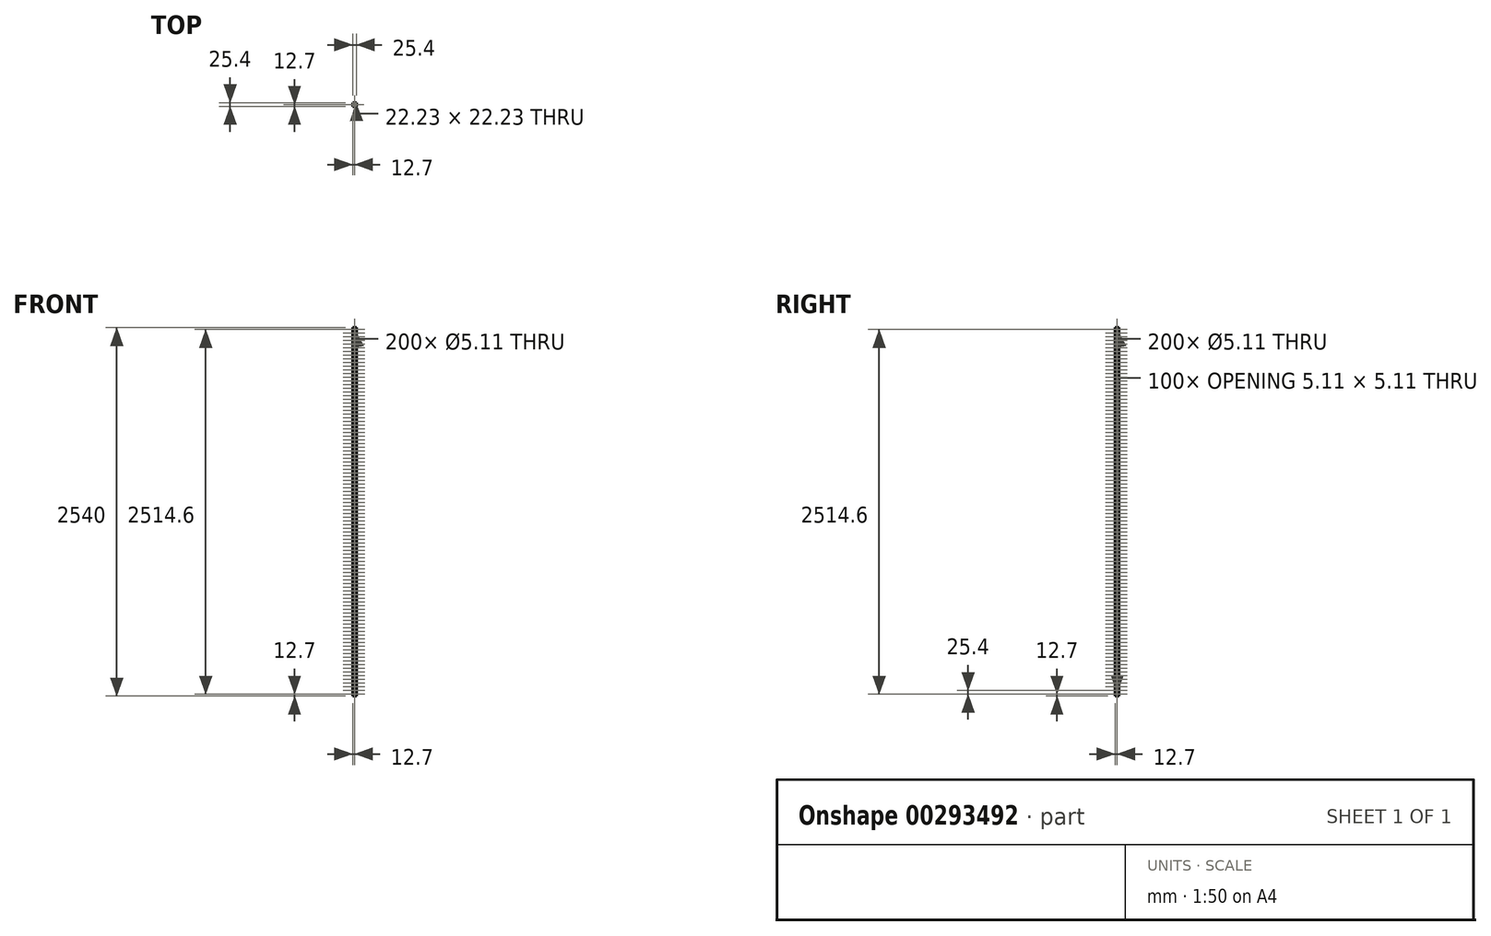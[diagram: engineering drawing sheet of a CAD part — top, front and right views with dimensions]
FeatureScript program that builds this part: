
annotation { "Feature Type Name" : "Feature", "Feature Type Description" : "" }
export const myFeature = defineFeature(function(context is Context, id is Id, definition is map)
    precondition{}
    {
        {
            var Q0;
            Q0=qCreatedBy(makeId("Top.planeOp"),FACE);
            var sketch = newSketch(context, id + "F0", { "sketchPlane" : qUnion([Q0])});
            skLineSegment(sketch, "E0.bottom", {"start": v(12.7, -12.7) * mm, "end": v(-12.7, -12.7) * mm});
            skLineSegment(sketch, "E0.top", {"start": v(12.7, 12.7) * mm, "end": v(-12.7, 12.7) * mm});
            skLineSegment(sketch, "E0.left", {"start": v(12.7, -12.7) * mm, "end": v(12.7, 12.7) * mm});
            skLineSegment(sketch, "E0.right", {"start": v(-12.7, -12.7) * mm, "end": v(-12.7, 12.7) * mm});
            skPoint(sketch, "E0.middle", {"position": v(0, 0) * mm});
            skSolve(sketch);
        }
        {
            var Q0;
            Q0=makeQuery(id+"F0.imprint","IMPRINT",FACE,{"disambiguationData":[TD([[makeQuery(id+"F0.imprint","IMPRINT",EDGE,{"derivedFrom":sQuery(id+"F0.wireOp",EDGE,"E0.bottom")}),-1.0]])]});
            extrude(context, id + "F1", {"entities" : qUnion([Q0]), "depth" : 2540 * mm});
        }
        {
            var Q0;
            Q0=makeQuery(id+"F1.opExtrude","SWEPT_FACE",FACE,{"disambiguationData":[OSD([sQuery(id+"F0.wireOp",EDGE,"E0.top")])]});
            var sketch = newSketch(context, id + "F2", { "sketchPlane" : qUnion([Q0])});
            skCircle(sketch, "E1", {"center": v(0, 2527.3) * mm, "radius": 2.55 * mm});
            skCircle(sketch, "E2.1.0.0", {"center": v(0, 2501.9) * mm, "radius": 2.55 * mm});
            skCircle(sketch, "E2.2.0.0", {"center": v(0, 2476.5) * mm, "radius": 2.55 * mm});
            skCircle(sketch, "E2.3.0.0", {"center": v(0, 2451.1) * mm, "radius": 2.55 * mm});
            skCircle(sketch, "E2.4.0.0", {"center": v(0, 2425.7) * mm, "radius": 2.55 * mm});
            skCircle(sketch, "E2.5.0.0", {"center": v(0, 2400.3) * mm, "radius": 2.55 * mm});
            skCircle(sketch, "E2.6.0.0", {"center": v(0, 2374.9) * mm, "radius": 2.55 * mm});
            skCircle(sketch, "E2.7.0.0", {"center": v(0, 2349.5) * mm, "radius": 2.55 * mm});
            skCircle(sketch, "E2.8.0.0", {"center": v(0, 2324.1) * mm, "radius": 2.55 * mm});
            skCircle(sketch, "E2.9.0.0", {"center": v(0, 2298.7) * mm, "radius": 2.55 * mm});
            skCircle(sketch, "E2.10.0.0", {"center": v(0, 2273.3) * mm, "radius": 2.55 * mm});
            skCircle(sketch, "E2.11.0.0", {"center": v(0, 2247.9) * mm, "radius": 2.55 * mm});
            skCircle(sketch, "E2.12.0.0", {"center": v(0, 2222.5) * mm, "radius": 2.55 * mm});
            skCircle(sketch, "E2.13.0.0", {"center": v(0, 2197.1) * mm, "radius": 2.55 * mm});
            skCircle(sketch, "E2.14.0.0", {"center": v(0, 2171.7) * mm, "radius": 2.55 * mm});
            skCircle(sketch, "E2.15.0.0", {"center": v(0, 2146.3) * mm, "radius": 2.55 * mm});
            skCircle(sketch, "E2.16.0.0", {"center": v(0, 2120.9) * mm, "radius": 2.55 * mm});
            skCircle(sketch, "E2.17.0.0", {"center": v(0, 2095.5) * mm, "radius": 2.55 * mm});
            skCircle(sketch, "E2.18.0.0", {"center": v(0, 2070.1) * mm, "radius": 2.55 * mm});
            skCircle(sketch, "E2.19.0.0", {"center": v(0, 2044.7) * mm, "radius": 2.55 * mm});
            skCircle(sketch, "E2.20.0.0", {"center": v(0, 2019.3) * mm, "radius": 2.55 * mm});
            skCircle(sketch, "E2.21.0.0", {"center": v(0, 1993.9) * mm, "radius": 2.55 * mm});
            skCircle(sketch, "E2.22.0.0", {"center": v(0, 1968.5) * mm, "radius": 2.55 * mm});
            skCircle(sketch, "E2.23.0.0", {"center": v(0, 1943.1) * mm, "radius": 2.55 * mm});
            skCircle(sketch, "E2.24.0.0", {"center": v(0, 1917.7) * mm, "radius": 2.55 * mm});
            skCircle(sketch, "E2.25.0.0", {"center": v(0, 1892.3) * mm, "radius": 2.55 * mm});
            skCircle(sketch, "E2.26.0.0", {"center": v(0, 1866.9) * mm, "radius": 2.55 * mm});
            skCircle(sketch, "E2.27.0.0", {"center": v(0, 1841.5) * mm, "radius": 2.55 * mm});
            skCircle(sketch, "E2.28.0.0", {"center": v(0, 1816.1) * mm, "radius": 2.55 * mm});
            skCircle(sketch, "E2.29.0.0", {"center": v(0, 1790.7) * mm, "radius": 2.55 * mm});
            skCircle(sketch, "E2.30.0.0", {"center": v(0, 1765.3) * mm, "radius": 2.55 * mm});
            skCircle(sketch, "E2.31.0.0", {"center": v(0, 1739.9) * mm, "radius": 2.55 * mm});
            skCircle(sketch, "E2.32.0.0", {"center": v(0, 1714.5) * mm, "radius": 2.55 * mm});
            skCircle(sketch, "E2.33.0.0", {"center": v(0, 1689.1) * mm, "radius": 2.55 * mm});
            skCircle(sketch, "E2.34.0.0", {"center": v(0, 1663.7) * mm, "radius": 2.55 * mm});
            skCircle(sketch, "E2.35.0.0", {"center": v(0, 1638.3) * mm, "radius": 2.55 * mm});
            skCircle(sketch, "E2.36.0.0", {"center": v(0, 1612.9) * mm, "radius": 2.55 * mm});
            skCircle(sketch, "E2.37.0.0", {"center": v(0, 1587.5) * mm, "radius": 2.55 * mm});
            skCircle(sketch, "E2.38.0.0", {"center": v(0, 1562.1) * mm, "radius": 2.55 * mm});
            skCircle(sketch, "E2.39.0.0", {"center": v(0, 1536.7) * mm, "radius": 2.55 * mm});
            skCircle(sketch, "E2.40.0.0", {"center": v(0, 1511.3) * mm, "radius": 2.55 * mm});
            skCircle(sketch, "E2.41.0.0", {"center": v(0, 1485.9) * mm, "radius": 2.55 * mm});
            skCircle(sketch, "E2.42.0.0", {"center": v(0, 1460.5) * mm, "radius": 2.55 * mm});
            skCircle(sketch, "E2.43.0.0", {"center": v(0, 1435.1) * mm, "radius": 2.55 * mm});
            skCircle(sketch, "E2.44.0.0", {"center": v(0, 1409.7) * mm, "radius": 2.55 * mm});
            skCircle(sketch, "E2.45.0.0", {"center": v(0, 1384.3) * mm, "radius": 2.55 * mm});
            skCircle(sketch, "E2.46.0.0", {"center": v(0, 1358.9) * mm, "radius": 2.55 * mm});
            skCircle(sketch, "E2.47.0.0", {"center": v(0, 1333.5) * mm, "radius": 2.55 * mm});
            skCircle(sketch, "E2.48.0.0", {"center": v(0, 1308.1) * mm, "radius": 2.55 * mm});
            skCircle(sketch, "E2.49.0.0", {"center": v(0, 1282.7) * mm, "radius": 2.55 * mm});
            skCircle(sketch, "E2.50.0.0", {"center": v(0, 1257.3) * mm, "radius": 2.55 * mm});
            skCircle(sketch, "E2.51.0.0", {"center": v(0, 1231.9) * mm, "radius": 2.55 * mm});
            skCircle(sketch, "E2.52.0.0", {"center": v(0, 1206.5) * mm, "radius": 2.55 * mm});
            skCircle(sketch, "E2.53.0.0", {"center": v(0, 1181.1) * mm, "radius": 2.55 * mm});
            skCircle(sketch, "E2.54.0.0", {"center": v(0, 1155.7) * mm, "radius": 2.55 * mm});
            skCircle(sketch, "E2.55.0.0", {"center": v(0, 1130.3) * mm, "radius": 2.55 * mm});
            skCircle(sketch, "E2.56.0.0", {"center": v(0, 1104.9) * mm, "radius": 2.55 * mm});
            skCircle(sketch, "E2.57.0.0", {"center": v(0, 1079.5) * mm, "radius": 2.55 * mm});
            skCircle(sketch, "E2.58.0.0", {"center": v(0, 1054.1) * mm, "radius": 2.55 * mm});
            skCircle(sketch, "E2.59.0.0", {"center": v(0, 1028.7) * mm, "radius": 2.55 * mm});
            skCircle(sketch, "E2.60.0.0", {"center": v(0, 1003.3) * mm, "radius": 2.55 * mm});
            skCircle(sketch, "E2.61.0.0", {"center": v(0, 977.9) * mm, "radius": 2.55 * mm});
            skCircle(sketch, "E2.62.0.0", {"center": v(0, 952.5) * mm, "radius": 2.55 * mm});
            skCircle(sketch, "E2.63.0.0", {"center": v(0, 927.1) * mm, "radius": 2.55 * mm});
            skCircle(sketch, "E2.64.0.0", {"center": v(0, 901.7) * mm, "radius": 2.55 * mm});
            skCircle(sketch, "E2.65.0.0", {"center": v(0, 876.3) * mm, "radius": 2.55 * mm});
            skCircle(sketch, "E2.66.0.0", {"center": v(0, 850.9) * mm, "radius": 2.55 * mm});
            skCircle(sketch, "E2.67.0.0", {"center": v(0, 825.5) * mm, "radius": 2.55 * mm});
            skCircle(sketch, "E2.68.0.0", {"center": v(0, 800.1) * mm, "radius": 2.55 * mm});
            skCircle(sketch, "E2.69.0.0", {"center": v(0, 774.7) * mm, "radius": 2.55 * mm});
            skCircle(sketch, "E2.70.0.0", {"center": v(0, 749.3) * mm, "radius": 2.55 * mm});
            skCircle(sketch, "E2.71.0.0", {"center": v(0, 723.9) * mm, "radius": 2.55 * mm});
            skCircle(sketch, "E2.72.0.0", {"center": v(0, 698.5) * mm, "radius": 2.55 * mm});
            skCircle(sketch, "E2.73.0.0", {"center": v(0, 673.1) * mm, "radius": 2.55 * mm});
            skCircle(sketch, "E2.74.0.0", {"center": v(0, 647.7) * mm, "radius": 2.55 * mm});
            skCircle(sketch, "E2.75.0.0", {"center": v(0, 622.3) * mm, "radius": 2.55 * mm});
            skCircle(sketch, "E2.76.0.0", {"center": v(0, 596.9) * mm, "radius": 2.55 * mm});
            skCircle(sketch, "E2.77.0.0", {"center": v(0, 571.5) * mm, "radius": 2.55 * mm});
            skCircle(sketch, "E2.78.0.0", {"center": v(0, 546.1) * mm, "radius": 2.55 * mm});
            skCircle(sketch, "E2.79.0.0", {"center": v(0, 520.7) * mm, "radius": 2.55 * mm});
            skCircle(sketch, "E2.80.0.0", {"center": v(0, 495.3) * mm, "radius": 2.55 * mm});
            skCircle(sketch, "E2.81.0.0", {"center": v(0, 469.9) * mm, "radius": 2.55 * mm});
            skCircle(sketch, "E2.82.0.0", {"center": v(0, 444.5) * mm, "radius": 2.55 * mm});
            skCircle(sketch, "E2.83.0.0", {"center": v(0, 419.1) * mm, "radius": 2.55 * mm});
            skCircle(sketch, "E2.84.0.0", {"center": v(0, 393.7) * mm, "radius": 2.55 * mm});
            skCircle(sketch, "E2.85.0.0", {"center": v(0, 368.3) * mm, "radius": 2.55 * mm});
            skCircle(sketch, "E2.86.0.0", {"center": v(0, 342.9) * mm, "radius": 2.55 * mm});
            skCircle(sketch, "E2.87.0.0", {"center": v(0, 317.5) * mm, "radius": 2.55 * mm});
            skCircle(sketch, "E2.88.0.0", {"center": v(0, 292.1) * mm, "radius": 2.55 * mm});
            skCircle(sketch, "E2.89.0.0", {"center": v(0, 266.7) * mm, "radius": 2.55 * mm});
            skCircle(sketch, "E2.90.0.0", {"center": v(0, 241.3) * mm, "radius": 2.55 * mm});
            skCircle(sketch, "E2.91.0.0", {"center": v(0, 215.9) * mm, "radius": 2.55 * mm});
            skCircle(sketch, "E2.92.0.0", {"center": v(0, 190.5) * mm, "radius": 2.55 * mm});
            skCircle(sketch, "E2.93.0.0", {"center": v(0, 165.1) * mm, "radius": 2.55 * mm});
            skCircle(sketch, "E2.94.0.0", {"center": v(0, 139.7) * mm, "radius": 2.55 * mm});
            skCircle(sketch, "E2.95.0.0", {"center": v(0, 114.3) * mm, "radius": 2.55 * mm});
            skCircle(sketch, "E2.96.0.0", {"center": v(0, 88.9) * mm, "radius": 2.55 * mm});
            skCircle(sketch, "E2.97.0.0", {"center": v(0, 63.5) * mm, "radius": 2.55 * mm});
            skCircle(sketch, "E2.98.0.0", {"center": v(0, 38.1) * mm, "radius": 2.55 * mm});
            skCircle(sketch, "E2.99.0.0", {"center": v(0, 12.7) * mm, "radius": 2.55 * mm});
            skLineSegment(sketch, "E2.direction1", {"start": v(0, 2527.3) * mm, "end": v(0, 2501.9) * mm, "construction": true});
            skSolve(sketch);
        }
        {
            var Q0;
            Q0=makeQuery(id+"F1.opExtrude","SWEPT_FACE",FACE,{"disambiguationData":[OSD([sQuery(id+"F0.wireOp",EDGE,"E0.right")])]});
            var sketch = newSketch(context, id + "F3", { "sketchPlane" : qUnion([Q0])});
            skCircle(sketch, "E3", {"center": v(0, 2527.3) * mm, "radius": 2.55 * mm});
            skCircle(sketch, "E4.1.0.0", {"center": v(0, 2501.9) * mm, "radius": 2.55 * mm});
            skCircle(sketch, "E4.2.0.0", {"center": v(0, 2476.5) * mm, "radius": 2.55 * mm});
            skCircle(sketch, "E4.3.0.0", {"center": v(0, 2451.1) * mm, "radius": 2.55 * mm});
            skCircle(sketch, "E4.4.0.0", {"center": v(0, 2425.7) * mm, "radius": 2.55 * mm});
            skCircle(sketch, "E4.5.0.0", {"center": v(0, 2400.3) * mm, "radius": 2.55 * mm});
            skCircle(sketch, "E4.6.0.0", {"center": v(0, 2374.9) * mm, "radius": 2.55 * mm});
            skCircle(sketch, "E4.7.0.0", {"center": v(0, 2349.5) * mm, "radius": 2.55 * mm});
            skCircle(sketch, "E4.8.0.0", {"center": v(0, 2324.1) * mm, "radius": 2.55 * mm});
            skCircle(sketch, "E4.9.0.0", {"center": v(0, 2298.7) * mm, "radius": 2.55 * mm});
            skCircle(sketch, "E4.10.0.0", {"center": v(0, 2273.3) * mm, "radius": 2.55 * mm});
            skCircle(sketch, "E4.11.0.0", {"center": v(0, 2247.9) * mm, "radius": 2.55 * mm});
            skCircle(sketch, "E4.12.0.0", {"center": v(0, 2222.5) * mm, "radius": 2.55 * mm});
            skCircle(sketch, "E4.13.0.0", {"center": v(0, 2197.1) * mm, "radius": 2.55 * mm});
            skCircle(sketch, "E4.14.0.0", {"center": v(0, 2171.7) * mm, "radius": 2.55 * mm});
            skCircle(sketch, "E4.15.0.0", {"center": v(0, 2146.3) * mm, "radius": 2.55 * mm});
            skCircle(sketch, "E4.16.0.0", {"center": v(0, 2120.9) * mm, "radius": 2.55 * mm});
            skCircle(sketch, "E4.17.0.0", {"center": v(0, 2095.5) * mm, "radius": 2.55 * mm});
            skCircle(sketch, "E4.18.0.0", {"center": v(0, 2070.1) * mm, "radius": 2.55 * mm});
            skCircle(sketch, "E4.19.0.0", {"center": v(0, 2044.7) * mm, "radius": 2.55 * mm});
            skCircle(sketch, "E4.20.0.0", {"center": v(0, 2019.3) * mm, "radius": 2.55 * mm});
            skCircle(sketch, "E4.21.0.0", {"center": v(0, 1993.9) * mm, "radius": 2.55 * mm});
            skCircle(sketch, "E4.22.0.0", {"center": v(0, 1968.5) * mm, "radius": 2.55 * mm});
            skCircle(sketch, "E4.23.0.0", {"center": v(0, 1943.1) * mm, "radius": 2.55 * mm});
            skCircle(sketch, "E4.24.0.0", {"center": v(0, 1917.7) * mm, "radius": 2.55 * mm});
            skCircle(sketch, "E4.25.0.0", {"center": v(0, 1892.3) * mm, "radius": 2.55 * mm});
            skCircle(sketch, "E4.26.0.0", {"center": v(0, 1866.9) * mm, "radius": 2.55 * mm});
            skCircle(sketch, "E4.27.0.0", {"center": v(0, 1841.5) * mm, "radius": 2.55 * mm});
            skCircle(sketch, "E4.28.0.0", {"center": v(0, 1816.1) * mm, "radius": 2.55 * mm});
            skCircle(sketch, "E4.29.0.0", {"center": v(0, 1790.7) * mm, "radius": 2.55 * mm});
            skCircle(sketch, "E4.30.0.0", {"center": v(0, 1765.3) * mm, "radius": 2.55 * mm});
            skCircle(sketch, "E4.31.0.0", {"center": v(0, 1739.9) * mm, "radius": 2.55 * mm});
            skCircle(sketch, "E4.32.0.0", {"center": v(0, 1714.5) * mm, "radius": 2.55 * mm});
            skCircle(sketch, "E4.33.0.0", {"center": v(0, 1689.1) * mm, "radius": 2.55 * mm});
            skCircle(sketch, "E4.34.0.0", {"center": v(0, 1663.7) * mm, "radius": 2.55 * mm});
            skCircle(sketch, "E4.35.0.0", {"center": v(0, 1638.3) * mm, "radius": 2.55 * mm});
            skCircle(sketch, "E4.36.0.0", {"center": v(0, 1612.9) * mm, "radius": 2.55 * mm});
            skCircle(sketch, "E4.37.0.0", {"center": v(0, 1587.5) * mm, "radius": 2.55 * mm});
            skCircle(sketch, "E4.38.0.0", {"center": v(0, 1562.1) * mm, "radius": 2.55 * mm});
            skCircle(sketch, "E4.39.0.0", {"center": v(0, 1536.7) * mm, "radius": 2.55 * mm});
            skCircle(sketch, "E4.40.0.0", {"center": v(0, 1511.3) * mm, "radius": 2.55 * mm});
            skCircle(sketch, "E4.41.0.0", {"center": v(0, 1485.9) * mm, "radius": 2.55 * mm});
            skCircle(sketch, "E4.42.0.0", {"center": v(0, 1460.5) * mm, "radius": 2.55 * mm});
            skCircle(sketch, "E4.43.0.0", {"center": v(0, 1435.1) * mm, "radius": 2.55 * mm});
            skCircle(sketch, "E4.44.0.0", {"center": v(0, 1409.7) * mm, "radius": 2.55 * mm});
            skCircle(sketch, "E4.45.0.0", {"center": v(0, 1384.3) * mm, "radius": 2.55 * mm});
            skCircle(sketch, "E4.46.0.0", {"center": v(0, 1358.9) * mm, "radius": 2.55 * mm});
            skCircle(sketch, "E4.47.0.0", {"center": v(0, 1333.5) * mm, "radius": 2.55 * mm});
            skCircle(sketch, "E4.48.0.0", {"center": v(0, 1308.1) * mm, "radius": 2.55 * mm});
            skCircle(sketch, "E4.49.0.0", {"center": v(0, 1282.7) * mm, "radius": 2.55 * mm});
            skCircle(sketch, "E4.50.0.0", {"center": v(0, 1257.3) * mm, "radius": 2.55 * mm});
            skCircle(sketch, "E4.51.0.0", {"center": v(0, 1231.9) * mm, "radius": 2.55 * mm});
            skCircle(sketch, "E4.52.0.0", {"center": v(0, 1206.5) * mm, "radius": 2.55 * mm});
            skCircle(sketch, "E4.53.0.0", {"center": v(0, 1181.1) * mm, "radius": 2.55 * mm});
            skCircle(sketch, "E4.54.0.0", {"center": v(0, 1155.7) * mm, "radius": 2.55 * mm});
            skCircle(sketch, "E4.55.0.0", {"center": v(0, 1130.3) * mm, "radius": 2.55 * mm});
            skCircle(sketch, "E4.56.0.0", {"center": v(0, 1104.9) * mm, "radius": 2.55 * mm});
            skCircle(sketch, "E4.57.0.0", {"center": v(0, 1079.5) * mm, "radius": 2.55 * mm});
            skCircle(sketch, "E4.58.0.0", {"center": v(0, 1054.1) * mm, "radius": 2.55 * mm});
            skCircle(sketch, "E4.59.0.0", {"center": v(0, 1028.7) * mm, "radius": 2.55 * mm});
            skCircle(sketch, "E4.60.0.0", {"center": v(0, 1003.3) * mm, "radius": 2.55 * mm});
            skCircle(sketch, "E4.61.0.0", {"center": v(0, 977.9) * mm, "radius": 2.55 * mm});
            skCircle(sketch, "E4.62.0.0", {"center": v(0, 952.5) * mm, "radius": 2.55 * mm});
            skCircle(sketch, "E4.63.0.0", {"center": v(0, 927.1) * mm, "radius": 2.55 * mm});
            skCircle(sketch, "E4.64.0.0", {"center": v(0, 901.7) * mm, "radius": 2.55 * mm});
            skCircle(sketch, "E4.65.0.0", {"center": v(0, 876.3) * mm, "radius": 2.55 * mm});
            skCircle(sketch, "E4.66.0.0", {"center": v(0, 850.9) * mm, "radius": 2.55 * mm});
            skCircle(sketch, "E4.67.0.0", {"center": v(0, 825.5) * mm, "radius": 2.55 * mm});
            skCircle(sketch, "E4.68.0.0", {"center": v(0, 800.1) * mm, "radius": 2.55 * mm});
            skCircle(sketch, "E4.69.0.0", {"center": v(0, 774.7) * mm, "radius": 2.55 * mm});
            skCircle(sketch, "E4.70.0.0", {"center": v(0, 749.3) * mm, "radius": 2.55 * mm});
            skCircle(sketch, "E4.71.0.0", {"center": v(0, 723.9) * mm, "radius": 2.55 * mm});
            skCircle(sketch, "E4.72.0.0", {"center": v(0, 698.5) * mm, "radius": 2.55 * mm});
            skCircle(sketch, "E4.73.0.0", {"center": v(0, 673.1) * mm, "radius": 2.55 * mm});
            skCircle(sketch, "E4.74.0.0", {"center": v(0, 647.7) * mm, "radius": 2.55 * mm});
            skCircle(sketch, "E4.75.0.0", {"center": v(0, 622.3) * mm, "radius": 2.55 * mm});
            skCircle(sketch, "E4.76.0.0", {"center": v(0, 596.9) * mm, "radius": 2.55 * mm});
            skCircle(sketch, "E4.77.0.0", {"center": v(0, 571.5) * mm, "radius": 2.55 * mm});
            skCircle(sketch, "E4.78.0.0", {"center": v(0, 546.1) * mm, "radius": 2.55 * mm});
            skCircle(sketch, "E4.79.0.0", {"center": v(0, 520.7) * mm, "radius": 2.55 * mm});
            skCircle(sketch, "E4.80.0.0", {"center": v(0, 495.3) * mm, "radius": 2.55 * mm});
            skCircle(sketch, "E4.81.0.0", {"center": v(0, 469.9) * mm, "radius": 2.55 * mm});
            skCircle(sketch, "E4.82.0.0", {"center": v(0, 444.5) * mm, "radius": 2.55 * mm});
            skCircle(sketch, "E4.83.0.0", {"center": v(0, 419.1) * mm, "radius": 2.55 * mm});
            skCircle(sketch, "E4.84.0.0", {"center": v(0, 393.7) * mm, "radius": 2.55 * mm});
            skCircle(sketch, "E4.85.0.0", {"center": v(0, 368.3) * mm, "radius": 2.55 * mm});
            skCircle(sketch, "E4.86.0.0", {"center": v(0, 342.9) * mm, "radius": 2.55 * mm});
            skCircle(sketch, "E4.87.0.0", {"center": v(0, 317.5) * mm, "radius": 2.55 * mm});
            skCircle(sketch, "E4.88.0.0", {"center": v(0, 292.1) * mm, "radius": 2.55 * mm});
            skCircle(sketch, "E4.89.0.0", {"center": v(0, 266.7) * mm, "radius": 2.55 * mm});
            skCircle(sketch, "E4.90.0.0", {"center": v(0, 241.3) * mm, "radius": 2.55 * mm});
            skCircle(sketch, "E4.91.0.0", {"center": v(0, 215.9) * mm, "radius": 2.55 * mm});
            skCircle(sketch, "E4.92.0.0", {"center": v(0, 190.5) * mm, "radius": 2.55 * mm});
            skCircle(sketch, "E4.93.0.0", {"center": v(0, 165.1) * mm, "radius": 2.55 * mm});
            skCircle(sketch, "E4.94.0.0", {"center": v(0, 139.7) * mm, "radius": 2.55 * mm});
            skCircle(sketch, "E4.95.0.0", {"center": v(0, 114.3) * mm, "radius": 2.55 * mm});
            skCircle(sketch, "E4.96.0.0", {"center": v(0, 88.9) * mm, "radius": 2.55 * mm});
            skCircle(sketch, "E4.97.0.0", {"center": v(0, 63.5) * mm, "radius": 2.55 * mm});
            skCircle(sketch, "E4.98.0.0", {"center": v(0, 38.1) * mm, "radius": 2.55 * mm});
            skCircle(sketch, "E4.99.0.0", {"center": v(0, 12.7) * mm, "radius": 2.55 * mm});
            skLineSegment(sketch, "E4.direction1", {"start": v(0, 2527.3) * mm, "end": v(0, 2501.9) * mm, "construction": true});
            skSolve(sketch);
        }
        {
            var Q0;
            Q0=makeQuery(id+"F1.opExtrude","CAP_FACE",FACE,{"disambiguationData":[OSD([sQuery(id+"F0.wireOp",EDGE,"E0.bottom"),sQuery(id+"F0.wireOp",EDGE,"E0.top"),sQuery(id+"F0.wireOp",EDGE,"E0.left"),sQuery(id+"F0.wireOp",EDGE,"E0.right")])],"isStart":false});
            var sketch = newSketch(context, id + "F4", { "sketchPlane" : qUnion([Q0])});
            skLineSegment(sketch, "E5.bottom", {"start": v(11.11, -11.11) * mm, "end": v(-11.11, -11.11) * mm});
            skLineSegment(sketch, "E5.top", {"start": v(11.11, 11.11) * mm, "end": v(-11.11, 11.11) * mm});
            skLineSegment(sketch, "E5.left", {"start": v(11.11, -11.11) * mm, "end": v(11.11, 11.11) * mm});
            skLineSegment(sketch, "E5.right", {"start": v(-11.11, -11.11) * mm, "end": v(-11.11, 11.11) * mm});
            skPoint(sketch, "E5.middle", {"position": v(0, 0) * mm});
            skSolve(sketch);
        }
        {
            var Q0;
            Q0=makeQuery(id+"F4.imprint","IMPRINT",FACE,{"disambiguationData":[TD([[makeQuery(id+"F4.imprint","IMPRINT",EDGE,{"derivedFrom":sQuery(id+"F4.wireOp",EDGE,"E5.bottom")}),-1.0]])]});
            extrude(context, id + "F5", {"entities" : qUnion([Q0]), "operationType" : NewBodyOperationType.REMOVE, "oppositeDirection" : true, "depth" : 2540 * mm});
        }
        {
            var Q0;
            Q0=sQuery(id+"F2.wireOp",VERTEX,"E2.99.0.0.center");
            var Q1;
            Q1=sQuery(id+"F2.wireOp",VERTEX,"E2.79.0.0.center");
            var Q2;
            Q2=sQuery(id+"F2.wireOp",VERTEX,"E2.63.0.0.center");
            var Q3;
            Q3=sQuery(id+"F2.wireOp",VERTEX,"E2.47.0.0.center");
            var Q4;
            Q4=sQuery(id+"F2.wireOp",VERTEX,"E2.31.0.0.center");
            var Q5;
            Q5=sQuery(id+"F2.wireOp",VERTEX,"E2.95.0.0.center");
            var Q6;
            Q6=sQuery(id+"F2.wireOp",VERTEX,"E2.54.0.0.center");
            var Q7;
            Q7=sQuery(id+"F2.wireOp",VERTEX,"E2.38.0.0.center");
            var Q8;
            Q8=sQuery(id+"F2.wireOp",VERTEX,"E2.22.0.0.center");
            var Q9;
            Q9=sQuery(id+"F2.wireOp",VERTEX,"E2.86.0.0.center");
            var Q10;
            Q10=sQuery(id+"F2.wireOp",VERTEX,"E2.70.0.0.center");
            var Q11;
            Q11=sQuery(id+"F2.wireOp",VERTEX,"E2.80.0.0.center");
            var Q12;
            Q12=sQuery(id+"F2.wireOp",VERTEX,"E2.13.0.0.center");
            var Q13;
            Q13=sQuery(id+"F2.wireOp",VERTEX,"E2.64.0.0.center");
            var Q14;
            Q14=sQuery(id+"F2.wireOp",VERTEX,"E2.96.0.0.center");
            var Q15;
            Q15=sQuery(id+"F2.wireOp",VERTEX,"E1.center");
            var Q16;
            Q16=sQuery(id+"F2.wireOp",VERTEX,"E2.1.0.0.center");
            var Q17;
            Q17=sQuery(id+"F2.wireOp",VERTEX,"E2.2.0.0.center");
            var Q18;
            Q18=sQuery(id+"F2.wireOp",VERTEX,"E2.3.0.0.center");
            var Q19;
            Q19=sQuery(id+"F2.wireOp",VERTEX,"E2.4.0.0.center");
            var Q20;
            Q20=sQuery(id+"F2.wireOp",VERTEX,"E2.5.0.0.center");
            var Q21;
            Q21=sQuery(id+"F2.wireOp",VERTEX,"E2.6.0.0.center");
            var Q22;
            Q22=sQuery(id+"F2.wireOp",VERTEX,"E2.8.0.0.center");
            var Q23;
            Q23=sQuery(id+"F2.wireOp",VERTEX,"E2.9.0.0.center");
            var Q24;
            Q24=sQuery(id+"F2.wireOp",VERTEX,"E2.10.0.0.center");
            var Q25;
            Q25=sQuery(id+"F2.wireOp",VERTEX,"E2.55.0.0.center");
            var Q26;
            Q26=sQuery(id+"F2.wireOp",VERTEX,"E2.39.0.0.center");
            var Q27;
            Q27=sQuery(id+"F2.wireOp",VERTEX,"E2.87.0.0.center");
            var Q28;
            Q28=sQuery(id+"F2.wireOp",VERTEX,"E2.71.0.0.center");
            var Q29;
            Q29=sQuery(id+"F2.wireOp",VERTEX,"E2.17.0.0.center");
            var Q30;
            Q30=sQuery(id+"F2.wireOp",VERTEX,"E2.49.0.0.center");
            var Q31;
            Q31=sQuery(id+"F2.wireOp",VERTEX,"E2.33.0.0.center");
            var Q32;
            Q32=sQuery(id+"F2.wireOp",VERTEX,"E2.56.0.0.center");
            var Q33;
            Q33=sQuery(id+"F2.wireOp",VERTEX,"E2.40.0.0.center");
            var Q34;
            Q34=sQuery(id+"F2.wireOp",VERTEX,"E2.24.0.0.center");
            var Q35;
            Q35=sQuery(id+"F2.wireOp",VERTEX,"E2.88.0.0.center");
            var Q36;
            Q36=sQuery(id+"F2.wireOp",VERTEX,"E2.72.0.0.center");
            var Q37;
            Q37=sQuery(id+"F2.wireOp",VERTEX,"E2.18.0.0.center");
            var Q38;
            Q38=sQuery(id+"F2.wireOp",VERTEX,"E2.82.0.0.center");
            var Q39;
            Q39=sQuery(id+"F2.wireOp",VERTEX,"E2.75.0.0.center");
            var Q40;
            Q40=sQuery(id+"F2.wireOp",VERTEX,"E2.66.0.0.center");
            var Q41;
            Q41=sQuery(id+"F2.wireOp",VERTEX,"E2.59.0.0.center");
            var Q42;
            Q42=sQuery(id+"F2.wireOp",VERTEX,"E2.50.0.0.center");
            var Q43;
            Q43=sQuery(id+"F2.wireOp",VERTEX,"E2.43.0.0.center");
            var Q44;
            Q44=sQuery(id+"F2.wireOp",VERTEX,"E2.34.0.0.center");
            var Q45;
            Q45=sQuery(id+"F2.wireOp",VERTEX,"E2.27.0.0.center");
            var Q46;
            Q46=sQuery(id+"F2.wireOp",VERTEX,"E2.98.0.0.center");
            var Q47;
            Q47=sQuery(id+"F2.wireOp",VERTEX,"E2.91.0.0.center");
            var Q48;
            Q48=sQuery(id+"F2.wireOp",VERTEX,"E2.58.0.0.center");
            var Q49;
            Q49=sQuery(id+"F2.wireOp",VERTEX,"E2.42.0.0.center");
            var Q50;
            Q50=sQuery(id+"F2.wireOp",VERTEX,"E2.26.0.0.center");
            var Q51;
            Q51=sQuery(id+"F2.wireOp",VERTEX,"E2.90.0.0.center");
            var Q52;
            Q52=sQuery(id+"F2.wireOp",VERTEX,"E2.74.0.0.center");
            var Q53;
            Q53=sQuery(id+"F2.wireOp",VERTEX,"E2.20.0.0.center");
            var Q54;
            Q54=sQuery(id+"F2.wireOp",VERTEX,"E2.77.0.0.center");
            var Q55;
            Q55=sQuery(id+"F2.wireOp",VERTEX,"E2.61.0.0.center");
            var Q56;
            Q56=sQuery(id+"F2.wireOp",VERTEX,"E2.45.0.0.center");
            var Q57;
            Q57=sQuery(id+"F2.wireOp",VERTEX,"E2.29.0.0.center");
            var Q58;
            Q58=sQuery(id+"F2.wireOp",VERTEX,"E2.93.0.0.center");
            var Q59;
            Q59=sQuery(id+"F2.wireOp",VERTEX,"E2.85.0.0.center");
            var Q60;
            Q60=sQuery(id+"F2.wireOp",VERTEX,"E2.69.0.0.center");
            var Q61;
            Q61=sQuery(id+"F2.wireOp",VERTEX,"E2.78.0.0.center");
            var Q62;
            Q62=sQuery(id+"F2.wireOp",VERTEX,"E2.62.0.0.center");
            var Q63;
            Q63=sQuery(id+"F2.wireOp",VERTEX,"E2.46.0.0.center");
            var Q64;
            Q64=sQuery(id+"F2.wireOp",VERTEX,"E2.30.0.0.center");
            var Q65;
            Q65=sQuery(id+"F2.wireOp",VERTEX,"E2.94.0.0.center");
            var Q66;
            Q66=sQuery(id+"F2.wireOp",VERTEX,"E2.53.0.0.center");
            var Q67;
            Q67=sQuery(id+"F2.wireOp",VERTEX,"E2.37.0.0.center");
            var Q68;
            Q68=sQuery(id+"F2.wireOp",VERTEX,"E2.21.0.0.center");
            var Q69;
            Q69=sQuery(id+"F2.wireOp",VERTEX,"E2.16.0.0.center");
            var Q70;
            Q70=sQuery(id+"F2.wireOp",VERTEX,"E2.12.0.0.center");
            var Q71;
            Q71=sQuery(id+"F2.wireOp",VERTEX,"E2.48.0.0.center");
            var Q72;
            Q72=sQuery(id+"F2.wireOp",VERTEX,"E2.32.0.0.center");
            var Q73;
            Q73=sQuery(id+"F2.wireOp",VERTEX,"E2.7.0.0.center");
            var Q74;
            Q74=sQuery(id+"F2.wireOp",VERTEX,"E2.23.0.0.center");
            var Q75;
            Q75=sQuery(id+"F2.wireOp",VERTEX,"E2.81.0.0.center");
            var Q76;
            Q76=sQuery(id+"F2.wireOp",VERTEX,"E2.65.0.0.center");
            var Q77;
            Q77=sQuery(id+"F2.wireOp",VERTEX,"E2.97.0.0.center");
            var Q78;
            Q78=sQuery(id+"F2.wireOp",VERTEX,"E2.57.0.0.center");
            var Q79;
            Q79=sQuery(id+"F2.wireOp",VERTEX,"E2.41.0.0.center");
            var Q80;
            Q80=sQuery(id+"F2.wireOp",VERTEX,"E2.25.0.0.center");
            var Q81;
            Q81=sQuery(id+"F2.wireOp",VERTEX,"E2.89.0.0.center");
            var Q82;
            Q82=sQuery(id+"F2.wireOp",VERTEX,"E2.73.0.0.center");
            var Q83;
            Q83=sQuery(id+"F2.wireOp",VERTEX,"E2.19.0.0.center");
            var Q84;
            Q84=sQuery(id+"F2.wireOp",VERTEX,"E2.76.0.0.center");
            var Q85;
            Q85=sQuery(id+"F2.wireOp",VERTEX,"E2.83.0.0.center");
            var Q86;
            Q86=sQuery(id+"F2.wireOp",VERTEX,"E2.60.0.0.center");
            var Q87;
            Q87=sQuery(id+"F2.wireOp",VERTEX,"E2.67.0.0.center");
            var Q88;
            Q88=sQuery(id+"F2.wireOp",VERTEX,"E2.44.0.0.center");
            var Q89;
            Q89=sQuery(id+"F2.wireOp",VERTEX,"E2.51.0.0.center");
            var Q90;
            Q90=sQuery(id+"F2.wireOp",VERTEX,"E2.28.0.0.center");
            var Q91;
            Q91=sQuery(id+"F2.wireOp",VERTEX,"E2.35.0.0.center");
            var Q92;
            Q92=sQuery(id+"F2.wireOp",VERTEX,"E2.92.0.0.center");
            var Q93;
            Q93=sQuery(id+"F2.wireOp",VERTEX,"E2.84.0.0.center");
            var Q94;
            Q94=sQuery(id+"F2.wireOp",VERTEX,"E2.68.0.0.center");
            var Q95;
            Q95=sQuery(id+"F2.wireOp",VERTEX,"E2.52.0.0.center");
            var Q96;
            Q96=sQuery(id+"F2.wireOp",VERTEX,"E2.36.0.0.center");
            var Q97;
            Q97=sQuery(id+"F2.wireOp",VERTEX,"E2.15.0.0.center");
            var Q98;
            Q98=sQuery(id+"F2.wireOp",VERTEX,"E2.11.0.0.center");
            var Q99;
            Q99=sQuery(id+"F2.wireOp",VERTEX,"E2.14.0.0.center");
            var Q100;
            Q100=makeQuery(id+"F1.opExtrude","SWEPT_BODY",BODY,{"disambiguationData":[OSD([sQuery(id+"F0.wireOp",EDGE,"E0.bottom"),sQuery(id+"F0.wireOp",EDGE,"E0.top"),sQuery(id+"F0.wireOp",EDGE,"E0.left"),sQuery(id+"F0.wireOp",EDGE,"E0.right")])]});
            hole(context, id + "F6", {"style" : HoleStyle.SIMPLE, "endStyle" : HoleEndStyle.THROUGH, "holeDiameter" : 5.1 * mm, "tappedDepth" : 12.7 * mm, "tapClearance" : 3, "locations" : qUnion([Q0, Q1, Q2, Q3, Q4, Q5, Q6, Q7, Q8, Q9, Q10, Q11, Q12, Q13, Q14, Q15, Q16, Q17, Q18, Q19, Q20, Q21, Q22, Q23, Q24, Q25, Q26, Q27, Q28, Q29, Q30, Q31, Q32, Q33, Q34, Q35, Q36, Q37, Q38, Q39, Q40, Q41, Q42, Q43, Q44, Q45, Q46, Q47, Q48, Q49, Q50, Q51, Q52, Q53, Q54, Q55, Q56, Q57, Q58, Q59, Q60, Q61, Q62, Q63, Q64, Q65, Q66, Q67, Q68, Q69, Q70, Q71, Q72, Q73, Q74, Q75, Q76, Q77, Q78, Q79, Q80, Q81, Q82, Q83, Q84, Q85, Q86, Q87, Q88, Q89, Q90, Q91, Q92, Q93, Q94, Q95, Q96, Q97, Q98, Q99]), "scope" : qUnion([Q100])});
        }
        {
            var Q0;
            Q0=sQuery(id+"F3.wireOp",VERTEX,"E4.48.0.0.center");
            var Q1;
            Q1=sQuery(id+"F3.wireOp",VERTEX,"E4.96.0.0.center");
            var Q2;
            Q2=sQuery(id+"F3.wireOp",VERTEX,"E4.55.0.0.center");
            var Q3;
            Q3=sQuery(id+"F3.wireOp",VERTEX,"E4.33.0.0.center");
            var Q4;
            Q4=sQuery(id+"F3.wireOp",VERTEX,"E4.97.0.0.center");
            var Q5;
            Q5=sQuery(id+"F3.wireOp",VERTEX,"E4.81.0.0.center");
            var Q6;
            Q6=sQuery(id+"F3.wireOp",VERTEX,"E4.65.0.0.center");
            var Q7;
            Q7=sQuery(id+"F3.wireOp",VERTEX,"E4.13.0.0.center");
            var Q8;
            Q8=sQuery(id+"F3.wireOp",VERTEX,"E3.center");
            var Q9;
            Q9=sQuery(id+"F3.wireOp",VERTEX,"E4.24.0.0.center");
            var Q10;
            Q10=sQuery(id+"F3.wireOp",VERTEX,"E4.2.0.0.center");
            var Q11;
            Q11=sQuery(id+"F3.wireOp",VERTEX,"E4.88.0.0.center");
            var Q12;
            Q12=sQuery(id+"F3.wireOp",VERTEX,"E4.3.0.0.center");
            var Q13;
            Q13=sQuery(id+"F3.wireOp",VERTEX,"E4.72.0.0.center");
            var Q14;
            Q14=sQuery(id+"F3.wireOp",VERTEX,"E4.40.0.0.center");
            var Q15;
            Q15=sQuery(id+"F3.wireOp",VERTEX,"E4.4.0.0.center");
            var Q16;
            Q16=sQuery(id+"F3.wireOp",VERTEX,"E4.5.0.0.center");
            var Q17;
            Q17=sQuery(id+"F3.wireOp",VERTEX,"E4.6.0.0.center");
            var Q18;
            Q18=sQuery(id+"F3.wireOp",VERTEX,"E4.7.0.0.center");
            var Q19;
            Q19=sQuery(id+"F3.wireOp",VERTEX,"E4.50.0.0.center");
            var Q20;
            Q20=sQuery(id+"F3.wireOp",VERTEX,"E4.34.0.0.center");
            var Q21;
            Q21=sQuery(id+"F3.wireOp",VERTEX,"E4.18.0.0.center");
            var Q22;
            Q22=sQuery(id+"F3.wireOp",VERTEX,"E4.9.0.0.center");
            var Q23;
            Q23=sQuery(id+"F3.wireOp",VERTEX,"E4.82.0.0.center");
            var Q24;
            Q24=sQuery(id+"F3.wireOp",VERTEX,"E4.66.0.0.center");
            var Q25;
            Q25=sQuery(id+"F3.wireOp",VERTEX,"E4.10.0.0.center");
            var Q26;
            Q26=sQuery(id+"F3.wireOp",VERTEX,"E4.25.0.0.center");
            var Q27;
            Q27=sQuery(id+"F3.wireOp",VERTEX,"E4.89.0.0.center");
            var Q28;
            Q28=sQuery(id+"F3.wireOp",VERTEX,"E4.73.0.0.center");
            var Q29;
            Q29=sQuery(id+"F3.wireOp",VERTEX,"E4.57.0.0.center");
            var Q30;
            Q30=sQuery(id+"F3.wireOp",VERTEX,"E4.41.0.0.center");
            var Q31;
            Q31=sQuery(id+"F3.wireOp",VERTEX,"E4.44.0.0.center");
            var Q32;
            Q32=sQuery(id+"F3.wireOp",VERTEX,"E4.51.0.0.center");
            var Q33;
            Q33=sQuery(id+"F3.wireOp",VERTEX,"E4.28.0.0.center");
            var Q34;
            Q34=sQuery(id+"F3.wireOp",VERTEX,"E4.35.0.0.center");
            var Q35;
            Q35=sQuery(id+"F3.wireOp",VERTEX,"E4.19.0.0.center");
            var Q36;
            Q36=sQuery(id+"F3.wireOp",VERTEX,"E4.92.0.0.center");
            var Q37;
            Q37=sQuery(id+"F3.wireOp",VERTEX,"E4.99.0.0.center");
            var Q38;
            Q38=sQuery(id+"F3.wireOp",VERTEX,"E4.76.0.0.center");
            var Q39;
            Q39=sQuery(id+"F3.wireOp",VERTEX,"E4.83.0.0.center");
            var Q40;
            Q40=sQuery(id+"F3.wireOp",VERTEX,"E4.60.0.0.center");
            var Q41;
            Q41=sQuery(id+"F3.wireOp",VERTEX,"E4.67.0.0.center");
            var Q42;
            Q42=sQuery(id+"F3.wireOp",VERTEX,"E4.68.0.0.center");
            var Q43;
            Q43=sQuery(id+"F3.wireOp",VERTEX,"E4.85.0.0.center");
            var Q44;
            Q44=sQuery(id+"F3.wireOp",VERTEX,"E4.69.0.0.center");
            var Q45;
            Q45=sQuery(id+"F3.wireOp",VERTEX,"E4.37.0.0.center");
            var Q46;
            Q46=sQuery(id+"F3.wireOp",VERTEX,"E4.21.0.0.center");
            var Q47;
            Q47=sQuery(id+"F3.wireOp",VERTEX,"E4.47.0.0.center");
            var Q48;
            Q48=sQuery(id+"F3.wireOp",VERTEX,"E4.95.0.0.center");
            var Q49;
            Q49=sQuery(id+"F3.wireOp",VERTEX,"E4.86.0.0.center");
            var Q50;
            Q50=sQuery(id+"F3.wireOp",VERTEX,"E4.54.0.0.center");
            var Q51;
            Q51=sQuery(id+"F3.wireOp",VERTEX,"E4.38.0.0.center");
            var Q52;
            Q52=sQuery(id+"F3.wireOp",VERTEX,"E4.32.0.0.center");
            var Q53;
            Q53=sQuery(id+"F3.wireOp",VERTEX,"E4.80.0.0.center");
            var Q54;
            Q54=sQuery(id+"F3.wireOp",VERTEX,"E4.64.0.0.center");
            var Q55;
            Q55=sQuery(id+"F3.wireOp",VERTEX,"E4.23.0.0.center");
            var Q56;
            Q56=sQuery(id+"F3.wireOp",VERTEX,"E4.87.0.0.center");
            var Q57;
            Q57=sQuery(id+"F3.wireOp",VERTEX,"E4.71.0.0.center");
            var Q58;
            Q58=sQuery(id+"F3.wireOp",VERTEX,"E4.39.0.0.center");
            var Q59;
            Q59=sQuery(id+"F3.wireOp",VERTEX,"E4.49.0.0.center");
            var Q60;
            Q60=sQuery(id+"F3.wireOp",VERTEX,"E4.17.0.0.center");
            var Q61;
            Q61=sQuery(id+"F3.wireOp",VERTEX,"E4.12.0.0.center");
            var Q62;
            Q62=sQuery(id+"F3.wireOp",VERTEX,"E4.1.0.0.center");
            var Q63;
            Q63=sQuery(id+"F3.wireOp",VERTEX,"E4.56.0.0.center");
            var Q64;
            Q64=sQuery(id+"F3.wireOp",VERTEX,"E4.8.0.0.center");
            var Q65;
            Q65=sQuery(id+"F3.wireOp",VERTEX,"E4.43.0.0.center");
            var Q66;
            Q66=sQuery(id+"F3.wireOp",VERTEX,"E4.27.0.0.center");
            var Q67;
            Q67=sQuery(id+"F3.wireOp",VERTEX,"E4.91.0.0.center");
            var Q68;
            Q68=sQuery(id+"F3.wireOp",VERTEX,"E4.98.0.0.center");
            var Q69;
            Q69=sQuery(id+"F3.wireOp",VERTEX,"E4.75.0.0.center");
            var Q70;
            Q70=sQuery(id+"F3.wireOp",VERTEX,"E4.59.0.0.center");
            var Q71;
            Q71=sQuery(id+"F3.wireOp",VERTEX,"E4.26.0.0.center");
            var Q72;
            Q72=sQuery(id+"F3.wireOp",VERTEX,"E4.90.0.0.center");
            var Q73;
            Q73=sQuery(id+"F3.wireOp",VERTEX,"E4.74.0.0.center");
            var Q74;
            Q74=sQuery(id+"F3.wireOp",VERTEX,"E4.58.0.0.center");
            var Q75;
            Q75=sQuery(id+"F3.wireOp",VERTEX,"E4.42.0.0.center");
            var Q76;
            Q76=sQuery(id+"F3.wireOp",VERTEX,"E4.45.0.0.center");
            var Q77;
            Q77=sQuery(id+"F3.wireOp",VERTEX,"E4.52.0.0.center");
            var Q78;
            Q78=sQuery(id+"F3.wireOp",VERTEX,"E4.36.0.0.center");
            var Q79;
            Q79=sQuery(id+"F3.wireOp",VERTEX,"E4.20.0.0.center");
            var Q80;
            Q80=sQuery(id+"F3.wireOp",VERTEX,"E4.93.0.0.center");
            var Q81;
            Q81=sQuery(id+"F3.wireOp",VERTEX,"E4.84.0.0.center");
            var Q82;
            Q82=sQuery(id+"F3.wireOp",VERTEX,"E4.61.0.0.center");
            var Q83;
            Q83=sQuery(id+"F3.wireOp",VERTEX,"E4.53.0.0.center");
            var Q84;
            Q84=sQuery(id+"F3.wireOp",VERTEX,"E4.46.0.0.center");
            var Q85;
            Q85=sQuery(id+"F3.wireOp",VERTEX,"E4.30.0.0.center");
            var Q86;
            Q86=sQuery(id+"F3.wireOp",VERTEX,"E4.94.0.0.center");
            var Q87;
            Q87=sQuery(id+"F3.wireOp",VERTEX,"E4.78.0.0.center");
            var Q88;
            Q88=sQuery(id+"F3.wireOp",VERTEX,"E4.62.0.0.center");
            var Q89;
            Q89=sQuery(id+"F3.wireOp",VERTEX,"E4.31.0.0.center");
            var Q90;
            Q90=sQuery(id+"F3.wireOp",VERTEX,"E4.79.0.0.center");
            var Q91;
            Q91=sQuery(id+"F3.wireOp",VERTEX,"E4.63.0.0.center");
            var Q92;
            Q92=sQuery(id+"F3.wireOp",VERTEX,"E4.22.0.0.center");
            var Q93;
            Q93=sQuery(id+"F3.wireOp",VERTEX,"E4.70.0.0.center");
            var Q94;
            Q94=sQuery(id+"F3.wireOp",VERTEX,"E4.16.0.0.center");
            var Q95;
            Q95=sQuery(id+"F3.wireOp",VERTEX,"E4.11.0.0.center");
            var Q96;
            Q96=sQuery(id+"F3.wireOp",VERTEX,"E4.29.0.0.center");
            var Q97;
            Q97=sQuery(id+"F3.wireOp",VERTEX,"E4.77.0.0.center");
            var Q98;
            Q98=sQuery(id+"F3.wireOp",VERTEX,"E4.14.0.0.center");
            var Q99;
            Q99=sQuery(id+"F3.wireOp",VERTEX,"E4.15.0.0.center");
            var Q100;
            Q100=makeQuery(id+"F1.opExtrude","SWEPT_BODY",BODY,{"disambiguationData":[OSD([sQuery(id+"F0.wireOp",EDGE,"E0.bottom"),sQuery(id+"F0.wireOp",EDGE,"E0.top"),sQuery(id+"F0.wireOp",EDGE,"E0.left"),sQuery(id+"F0.wireOp",EDGE,"E0.right")])]});
            hole(context, id + "F7", {"style" : HoleStyle.SIMPLE, "endStyle" : HoleEndStyle.THROUGH, "holeDiameter" : 5.1 * mm, "tappedDepth" : 12.7 * mm, "tapClearance" : 3, "locations" : qUnion([Q0, Q1, Q2, Q3, Q4, Q5, Q6, Q7, Q8, Q9, Q10, Q11, Q12, Q13, Q14, Q15, Q16, Q17, Q18, Q19, Q20, Q21, Q22, Q23, Q24, Q25, Q26, Q27, Q28, Q29, Q30, Q31, Q32, Q33, Q34, Q35, Q36, Q37, Q38, Q39, Q40, Q41, Q42, Q43, Q44, Q45, Q46, Q47, Q48, Q49, Q50, Q51, Q52, Q53, Q54, Q55, Q56, Q57, Q58, Q59, Q60, Q61, Q62, Q63, Q64, Q65, Q66, Q67, Q68, Q69, Q70, Q71, Q72, Q73, Q74, Q75, Q76, Q77, Q78, Q79, Q80, Q81, Q82, Q83, Q84, Q85, Q86, Q87, Q88, Q89, Q90, Q91, Q92, Q93, Q94, Q95, Q96, Q97, Q98, Q99]), "scope" : qUnion([Q100])});
        }
    });
